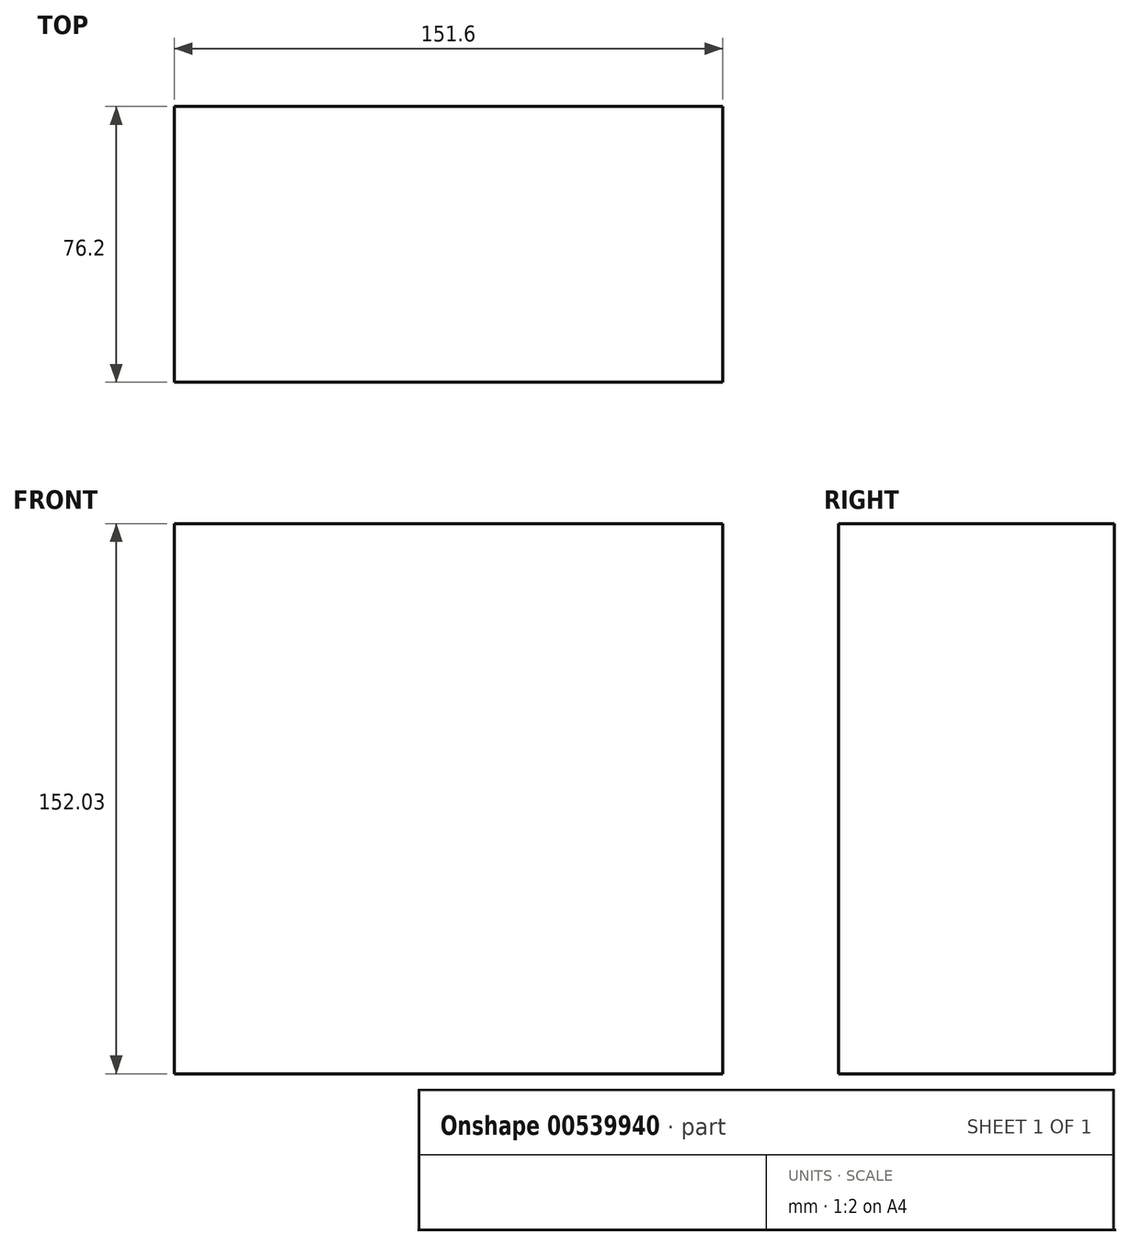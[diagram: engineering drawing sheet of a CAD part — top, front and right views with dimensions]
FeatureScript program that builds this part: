
annotation { "Feature Type Name" : "Feature", "Feature Type Description" : "" }
export const myFeature = defineFeature(function(context is Context, id is Id, definition is map)
    precondition{}
    {
        {
            var Q0;
            Q0=qCreatedBy(makeId("Front.planeOp"),FACE);
            var sketch = newSketch(context, id + "F0", { "sketchPlane" : qUnion([Q0])});
            skLineSegment(sketch, "E0.bottom", {"start": v(-75.98, 75.84) * mm, "end": v(75.62, 75.84) * mm});
            skLineSegment(sketch, "E0.top", {"start": v(-75.98, -76.2) * mm, "end": v(75.62, -76.2) * mm});
            skLineSegment(sketch, "E0.left", {"start": v(-75.98, 75.84) * mm, "end": v(-75.98, -76.2) * mm});
            skLineSegment(sketch, "E0.right", {"start": v(75.62, 75.84) * mm, "end": v(75.62, -76.2) * mm});
            skSolve(sketch);
        }
        {
            var Q0;
            Q0=makeQuery(id+"F0.imprint","IMPRINT",FACE,{"disambiguationData":[TD([[makeQuery(id+"F0.imprint","IMPRINT",EDGE,{"derivedFrom":sQuery(id+"F0.wireOp",EDGE,"E0.bottom")}),-1.0]])]});
            extrude(context, id + "F1", {"entities" : qUnion([Q0]), "depth" : 76.2 * mm, "offsetDistance" : 25.4 * mm});
        }
        {
            var Q0;
            Q0=makeQuery(id+"F1.opExtrude","CAP_FACE",FACE,{"disambiguationData":[OSD([sQuery(id+"F0.wireOp",EDGE,"E0.bottom"),sQuery(id+"F0.wireOp",EDGE,"E0.top"),sQuery(id+"F0.wireOp",EDGE,"E0.left"),sQuery(id+"F0.wireOp",EDGE,"E0.right")])],"isStart":false});
            var sketch = newSketch(context, id + "F2", { "sketchPlane" : qUnion([Q0])});
            skLineSegment(sketch, "E1.bottom", {"start": v(-31.46, 21.2) * mm, "end": v(44.74, 21.2) * mm});
            skLineSegment(sketch, "E1.top", {"start": v(-31.46, -16.9) * mm, "end": v(44.74, -16.9) * mm});
            skLineSegment(sketch, "E1.left", {"start": v(-31.46, 21.2) * mm, "end": v(-31.46, -16.9) * mm});
            skLineSegment(sketch, "E1.right", {"start": v(44.74, 21.2) * mm, "end": v(44.74, -16.9) * mm});
            skLineSegment(sketch, "E2.left", {"start": v(6.64, 21.2) * mm, "end": v(6.64, 21.2) * mm});
            skSolve(sketch);
        }
    });
